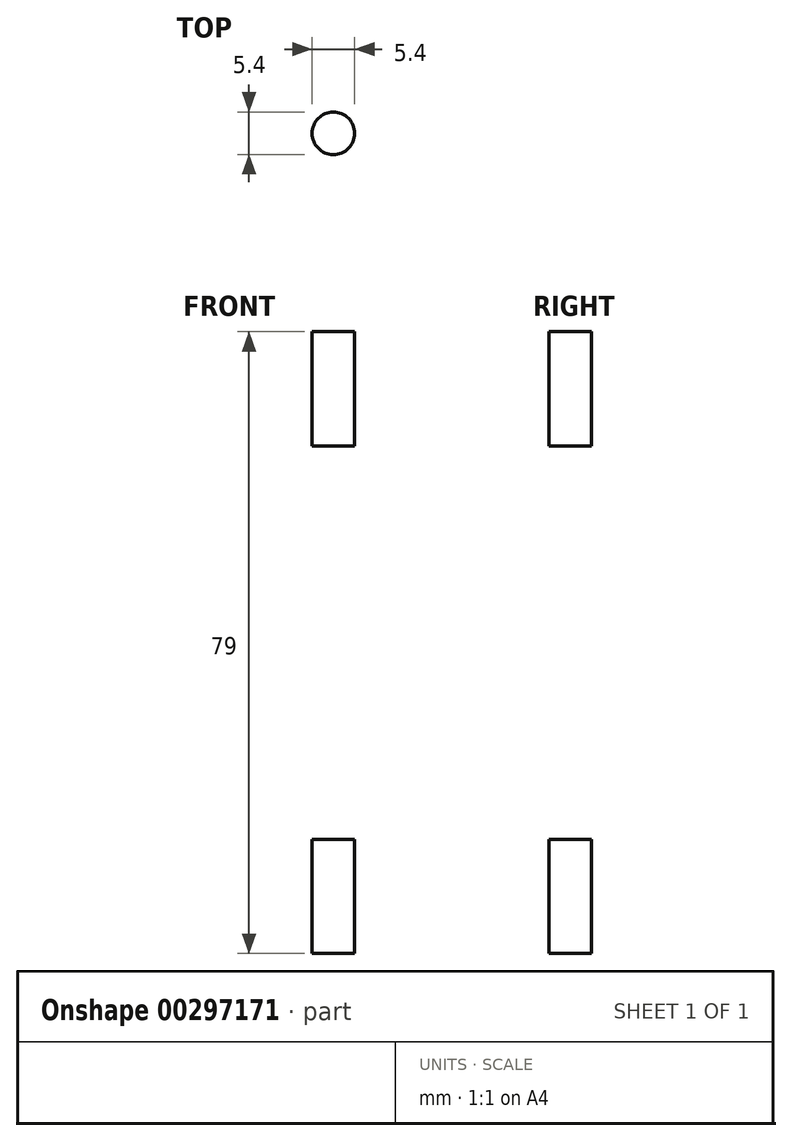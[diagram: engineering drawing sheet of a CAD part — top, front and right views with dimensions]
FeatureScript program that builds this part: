
annotation { "Feature Type Name" : "Feature", "Feature Type Description" : "" }
export const myFeature = defineFeature(function(context is Context, id is Id, definition is map)
    precondition{}
    {
        {
            var Q0;
            Q0=qCreatedBy(makeId("Top.planeOp"),FACE);
            var sketch = newSketch(context, id + "F0", { "sketchPlane" : qUnion([Q0])});
            skLineSegment(sketch, "E0.bottom", {"start": v(-23, 7) * mm, "end": v(-9, 7) * mm});
            skLineSegment(sketch, "E0.top", {"start": v(-23, -7) * mm, "end": v(-9, -7) * mm});
            skLineSegment(sketch, "E0.left", {"start": v(-23, 7) * mm, "end": v(-23, -7) * mm});
            skLineSegment(sketch, "E0.right", {"start": v(23, 7) * mm, "end": v(23, -7) * mm});
            skPoint(sketch, "E0.middle", {"position": v(0, 0) * mm});
            skLineSegment(sketch, "E1.bottom", {"start": v(-9, 15) * mm, "end": v(9, 15) * mm});
            skLineSegment(sketch, "E1.top", {"start": v(-9, -15) * mm, "end": v(9, -15) * mm});
            skLineSegment(sketch, "E2", {"start": v(9, 15) * mm, "end": v(9, 7) * mm});
            skLineSegment(sketch, "E3", {"start": v(9, -15) * mm, "end": v(9, -7) * mm});
            skLineSegment(sketch, "E4.trimOffspring", {"start": v(9, 7) * mm, "end": v(23, 7) * mm});
            skLineSegment(sketch, "E5.trimOffspring", {"start": v(9, -7) * mm, "end": v(23, -7) * mm});
            skLineSegment(sketch, "E6", {"start": v(-9, 15) * mm, "end": v(-9, 7) * mm});
            skLineSegment(sketch, "E7", {"start": v(-9, -7) * mm, "end": v(-9, -15) * mm});
            skSolve(sketch);
        }
        {
            var Q0;
            Q0 = qSketchRegion(id + "F0", true);
            extrude(context, id + "F1", {"entities" : qUnion([Q0]), "depth" : 79 * mm, "offsetDistance" : 25 * mm});
        }
        {
            var Q0;
            Q0=makeQuery(id+"F1.opExtrude","SWEPT_FACE",FACE,{"disambiguationData":[OSD([sQuery(id+"F0.wireOp",EDGE,"E0.top")])]});
            var sketch = newSketch(context, id + "F2", { "sketchPlane" : qUnion([Q0])});
            skLineSegment(sketch, "E8.top", {"start": v(-9, 63) * mm, "end": v(-23, 63) * mm});
            skLineSegment(sketch, "E8.left", {"start": v(-9, 39.5) * mm, "end": v(-9, 63) * mm});
            skLineSegment(sketch, "E9", {"start": v(-23, 16) * mm, "end": v(-9, 16) * mm});
            skLineSegment(sketch, "E10", {"start": v(-9, 16) * mm, "end": v(-9, 39.5) * mm});
            skLineSegment(sketch, "E11.MirrorCS", {"start": v(9, 16) * mm, "end": v(9, 39.5) * mm});
            skLineSegment(sketch, "E12.MirrorCS", {"start": v(23, 16) * mm, "end": v(9, 16) * mm});
            skLineSegment(sketch, "E13.MirrorCS", {"start": v(9, 63) * mm, "end": v(23, 63) * mm});
            skLineSegment(sketch, "E14.MirrorCS", {"start": v(9, 39.5) * mm, "end": v(9, 63) * mm});
            skLineSegment(sketch, "E15", {"start": v(-23, 63) * mm, "end": v(-9, 39.5) * mm});
            skLineSegment(sketch, "E16", {"start": v(-9, 39.5) * mm, "end": v(-23, 16) * mm});
            skLineSegment(sketch, "E17.MirrorCS", {"start": v(9, 39.5) * mm, "end": v(23, 16) * mm});
            skLineSegment(sketch, "E18.MirrorCS", {"start": v(23, 63) * mm, "end": v(9, 39.5) * mm});
            skLineSegment(sketch, "E19", {"start": v(23, 63) * mm, "end": v(23, 16) * mm});
            skSolve(sketch);
        }
        {
            var Q0;
            {var subQ0=sQuery(id+"F2.wireOp",EDGE,"E15");Q0=makeQuery(id+"F2.imprint","IMPRINT",FACE,{"disambiguationData":[TD([[makeQuery(id+"F2.imprint","IMPRINT",EDGE,{"derivedFrom":subQ0}),-1.0]])]});}
            var Q1;
            Q1=makeQuery(id+"F2.imprint","IMPRINT",FACE,{"disambiguationData":[TD([[makeQuery(id+"F2.imprint","IMPRINT",EDGE,{"derivedFrom":sQuery(id+"F2.wireOp",EDGE,"E17.MirrorCS")}),1.0]])]});
            extrude(context, id + "F3", {"entities" : qUnion([Q0, Q1]), "operationType" : NewBodyOperationType.REMOVE, "endBound" : BoundingType.UP_TO_NEXT, "oppositeDirection" : true, "depth" : 25 * mm});
        }
        {
            var Q0;
            Q0=makeQuery(id+"F1.opExtrude","CAP_FACE",FACE,{"disambiguationData":[OSD([sQuery(id+"F0.wireOp",EDGE,"E0.bottom"),sQuery(id+"F0.wireOp",EDGE,"E0.top"),sQuery(id+"F0.wireOp",EDGE,"E0.left"),sQuery(id+"F0.wireOp",EDGE,"E0.right"),sQuery(id+"F0.wireOp",EDGE,"E1.bottom"),sQuery(id+"F0.wireOp",EDGE,"E1.top"),sQuery(id+"F0.wireOp",EDGE,"E2"),sQuery(id+"F0.wireOp",EDGE,"E3"),sQuery(id+"F0.wireOp",EDGE,"E4.trimOffspring"),sQuery(id+"F0.wireOp",EDGE,"E5.trimOffspring"),sQuery(id+"F0.wireOp",EDGE,"E6"),sQuery(id+"F0.wireOp",EDGE,"E7")])],"isStart":false});
            var sketch = newSketch(context, id + "F4", { "sketchPlane" : qUnion([Q0])});
            skCircle(sketch, "E20", {"center": v(-16, 0) * mm, "radius": 2.7 * mm});
            skCircle(sketch, "E21.MirrorC", {"center": v(16, 0) * mm, "radius": 2.7 * mm});
            skSolve(sketch);
        }
        {
            var Q0;
            Q0=makeQuery(id+"F4.imprint","IMPRINT",FACE,{"disambiguationData":[TD([[makeQuery(id+"F4.imprint","IMPRINT",EDGE,{"derivedFrom":sQuery(id+"F4.wireOp",EDGE,"E20")}),1.0]])]});
            var Q1;
            Q1=makeQuery(id+"F4.imprint","IMPRINT",FACE,{"disambiguationData":[TD([[makeQuery(id+"F4.imprint","IMPRINT",EDGE,{"derivedFrom":sQuery(id+"F4.wireOp",EDGE,"E21.MirrorC")}),-1.0]])]});
            extrude(context, id + "F5", {"entities" : qUnion([Q0, Q1]), "operationType" : NewBodyOperationType.REMOVE, "oppositeDirection" : true, "depth" : 79 * mm});
        }
        {
            var Q0;
            Q0=qCreatedBy(makeId("Top.planeOp"),FACE);
            cPlane(context, id + "F6", {"entities" : qUnion([Q0]), "cplaneType" : CPlaneType.OFFSET, "offset" : 39.5 * mm, "width" : 150 * mm, "height" : 150 * mm});
        }
        {
            var Q0;
            Q0=qCreatedBy(id+"F6.planeOp",FACE);
            var sketch = newSketch(context, id + "F7", { "sketchPlane" : qUnion([Q0])});
            skCircle(sketch, "E22.cCircle", {"center": v(-16, 0) * mm, "radius": 4.25 * mm, "construction": true});
            skLineSegment(sketch, "E22.0", {"start": v(-20.25, 2.45) * mm, "end": v(-16, 4.9) * mm});
            skLineSegment(sketch, "E22.1", {"start": v(-16, 4.9) * mm, "end": v(-11.75, 2.45) * mm});
            skLineSegment(sketch, "E22.2", {"start": v(-11.75, 2.45) * mm, "end": v(-11.75, -2.45) * mm});
            skLineSegment(sketch, "E22.3", {"start": v(-11.75, -2.45) * mm, "end": v(-16, -4.9) * mm});
            skLineSegment(sketch, "E22.4", {"start": v(-16, -4.9) * mm, "end": v(-20.25, -2.45) * mm});
            skLineSegment(sketch, "E22.5", {"start": v(-20.25, -2.45) * mm, "end": v(-20.25, 2.45) * mm});
            skPoint(sketch, "E22.0.midPoint", {"position": v(-18.13, 3.68) * mm});
            skCircle(sketch, "E23.MirrorC", {"center": v(16, 0) * mm, "radius": 4.25 * mm, "construction": true});
            skLineSegment(sketch, "E24.MirrorCS", {"start": v(20.25, 2.45) * mm, "end": v(16, 4.9) * mm});
            skLineSegment(sketch, "E25.MirrorCS", {"start": v(16, -4.9) * mm, "end": v(20.25, -2.45) * mm});
            skLineSegment(sketch, "E26.MirrorCS", {"start": v(11.75, -2.45) * mm, "end": v(16, -4.9) * mm});
            skLineSegment(sketch, "E27.MirrorCS", {"start": v(11.75, 2.45) * mm, "end": v(11.75, -2.45) * mm});
            skPoint(sketch, "E28.MirrorP", {"position": v(18.13, 3.68) * mm});
            skLineSegment(sketch, "E29.MirrorCS", {"start": v(16, 4.9) * mm, "end": v(11.75, 2.45) * mm});
            skLineSegment(sketch, "E30.MirrorCS", {"start": v(20.25, -2.45) * mm, "end": v(20.25, 2.45) * mm});
            skSolve(sketch);
        }
        {
            var Q0;
            Q0 = qSketchRegion(id + "F7", true);
            extrude(context, id + "F8", {"entities" : qUnion([Q0]), "operationType" : NewBodyOperationType.REMOVE, "oppositeDirection" : true, "depth" : 25 * mm, "hasSecondDirection" : true, "secondDirectionOppositeDirection" : false, "secondDirectionDepth" : 25 * mm});
        }
    });
